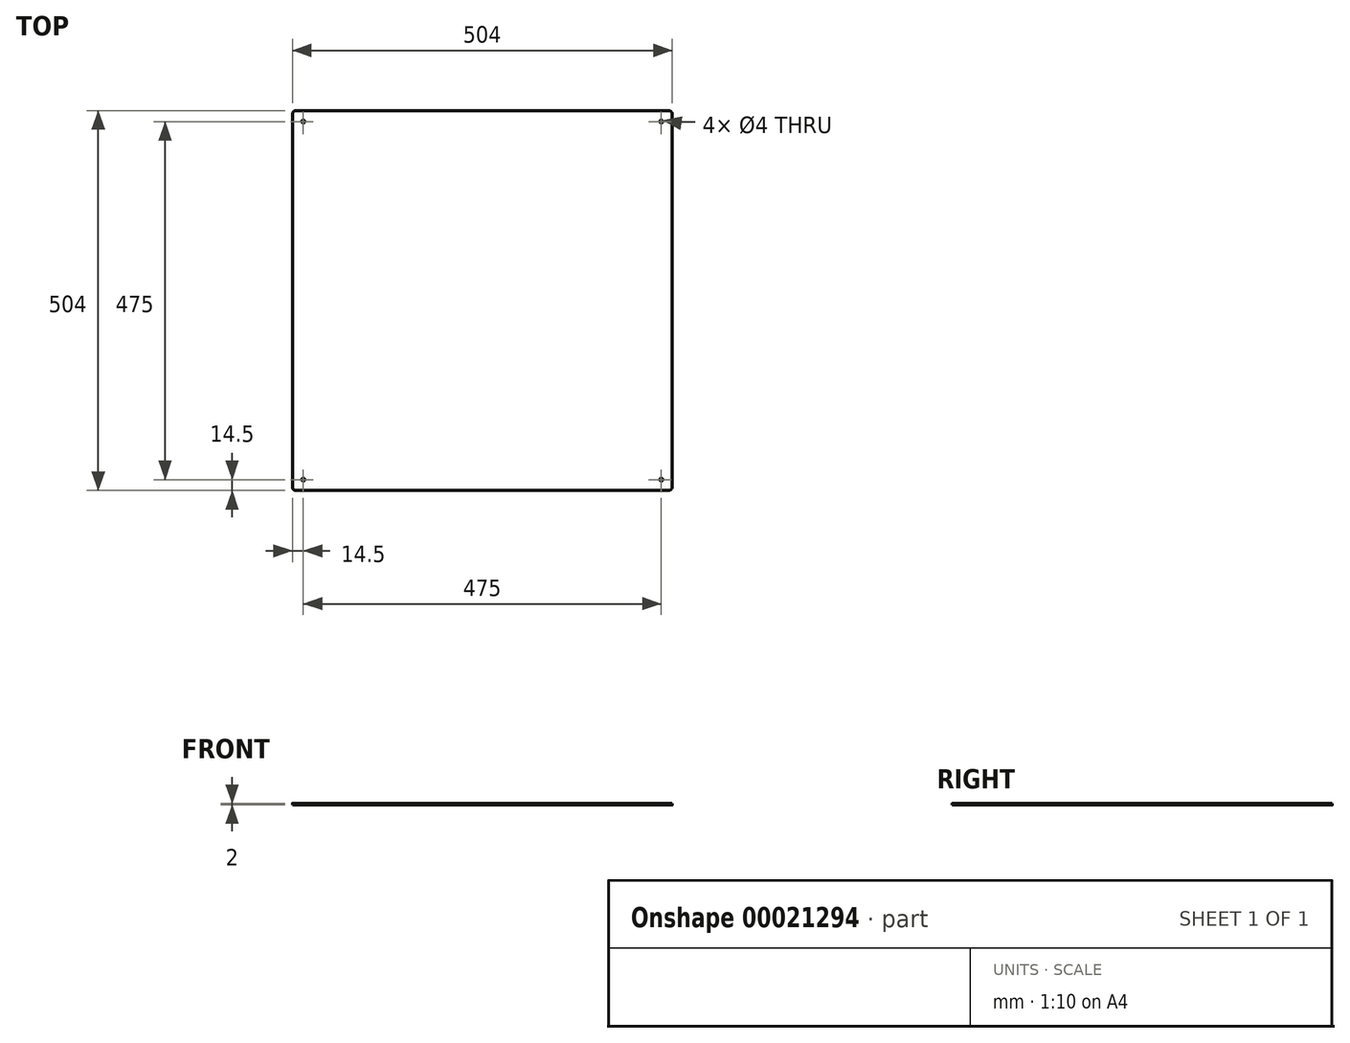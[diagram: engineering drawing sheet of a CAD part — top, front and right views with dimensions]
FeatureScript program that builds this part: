
annotation { "Feature Type Name" : "Feature", "Feature Type Description" : "" }
export const myFeature = defineFeature(function(context is Context, id is Id, definition is map)
    precondition{}
    {
        {
            var Q0;
            Q0=qCreatedBy(makeId("Top.planeOp"),FACE);
            var sketch = newSketch(context, id + "F0", { "sketchPlane" : qUnion([Q0])});
            skLineSegment(sketch, "E0.rect.bottom", {"start": v(252, -252) * mm, "end": v(-252, -252) * mm});
            skLineSegment(sketch, "E0.rect.top", {"start": v(252, 252) * mm, "end": v(-252, 252) * mm});
            skLineSegment(sketch, "E0.rect.left", {"start": v(252, -252) * mm, "end": v(252, 252) * mm});
            skLineSegment(sketch, "E0.rect.right", {"start": v(-252, -252) * mm, "end": v(-252, 252) * mm});
            skPoint(sketch, "E0.rect.middle", {"position": v(0, 0) * mm});
            skSolve(sketch);
        }
        {
            var Q0;
            Q0 = qSketchRegion(id + "F0", true);
            extrude(context, id + "F1", {"entities" : qUnion([Q0]), "depth" : 2 * mm});
        }
        {
            var Q0;
            Q0=makeQuery(id+"F1.opExtrude","CAP_FACE",FACE,{"disambiguationData":[OSD([sQuery(id+"F0.wireOp",EDGE,"E0.rect.bottom"),sQuery(id+"F0.wireOp",EDGE,"E0.rect.top"),sQuery(id+"F0.wireOp",EDGE,"E0.rect.left"),sQuery(id+"F0.wireOp",EDGE,"E0.rect.right")])],"isStart":false});
            var sketch = newSketch(context, id + "F2", { "sketchPlane" : qUnion([Q0])});
            skLineSegment(sketch, "E1.rect.bottom", {"start": v(237.5, 237.5) * mm, "end": v(-237.5, 237.5) * mm, "construction": true});
            skLineSegment(sketch, "E1.rect.top", {"start": v(237.5, -237.5) * mm, "end": v(-237.5, -237.5) * mm, "construction": true});
            skLineSegment(sketch, "E1.rect.left", {"start": v(237.5, 237.5) * mm, "end": v(237.5, -237.5) * mm, "construction": true});
            skLineSegment(sketch, "E1.rect.right", {"start": v(-237.5, 237.5) * mm, "end": v(-237.5, -237.5) * mm, "construction": true});
            skPoint(sketch, "E1.rect.middle", {"position": v(0, 0) * mm});
            skCircle(sketch, "E2", {"center": v(-237.5, 237.5) * mm, "radius": 2 * mm});
            skCircle(sketch, "E3", {"center": v(237.5, 237.5) * mm, "radius": 2 * mm});
            skCircle(sketch, "E4", {"center": v(237.5, -237.5) * mm, "radius": 2 * mm});
            skCircle(sketch, "E5", {"center": v(-237.5, -237.5) * mm, "radius": 2 * mm});
            skSolve(sketch);
        }
        {
            var Q0;
            Q0 = qSketchRegion(id + "F2", true);
            extrude(context, id + "F3", {"entities" : qUnion([Q0]), "operationType" : NewBodyOperationType.REMOVE, "oppositeDirection" : true, "depth" : 25 * mm});
        }
        {
            var Q0;
            Q0=makeQuery(id+"F1.opExtrude","SWEPT_EDGE",EDGE,{"disambiguationData":[OSD([sQuery(id+"F0.wireOp",EDGE,"E0.rect.bottom"),sQuery(id+"F0.wireOp",EDGE,"E0.rect.right")])]});
            var Q1;
            Q1=makeQuery(id+"F1.opExtrude","SWEPT_EDGE",EDGE,{"disambiguationData":[OSD([sQuery(id+"F0.wireOp",EDGE,"E0.rect.bottom"),sQuery(id+"F0.wireOp",EDGE,"E0.rect.left")])]});
            var Q2;
            Q2=makeQuery(id+"F1.opExtrude","SWEPT_EDGE",EDGE,{"disambiguationData":[OSD([sQuery(id+"F0.wireOp",EDGE,"E0.rect.top"),sQuery(id+"F0.wireOp",EDGE,"E0.rect.left")])]});
            var Q3;
            Q3=makeQuery(id+"F1.opExtrude","SWEPT_EDGE",EDGE,{"disambiguationData":[OSD([sQuery(id+"F0.wireOp",EDGE,"E0.rect.top"),sQuery(id+"F0.wireOp",EDGE,"E0.rect.right")])]});
            fillet(context, id + "F4", {"entities" : qUnion([Q0, Q1, Q2, Q3]), "radius" : 5 * mm, "tangentPropagation" : true, "allowEdgeOverflow" : false});
        }
    });
